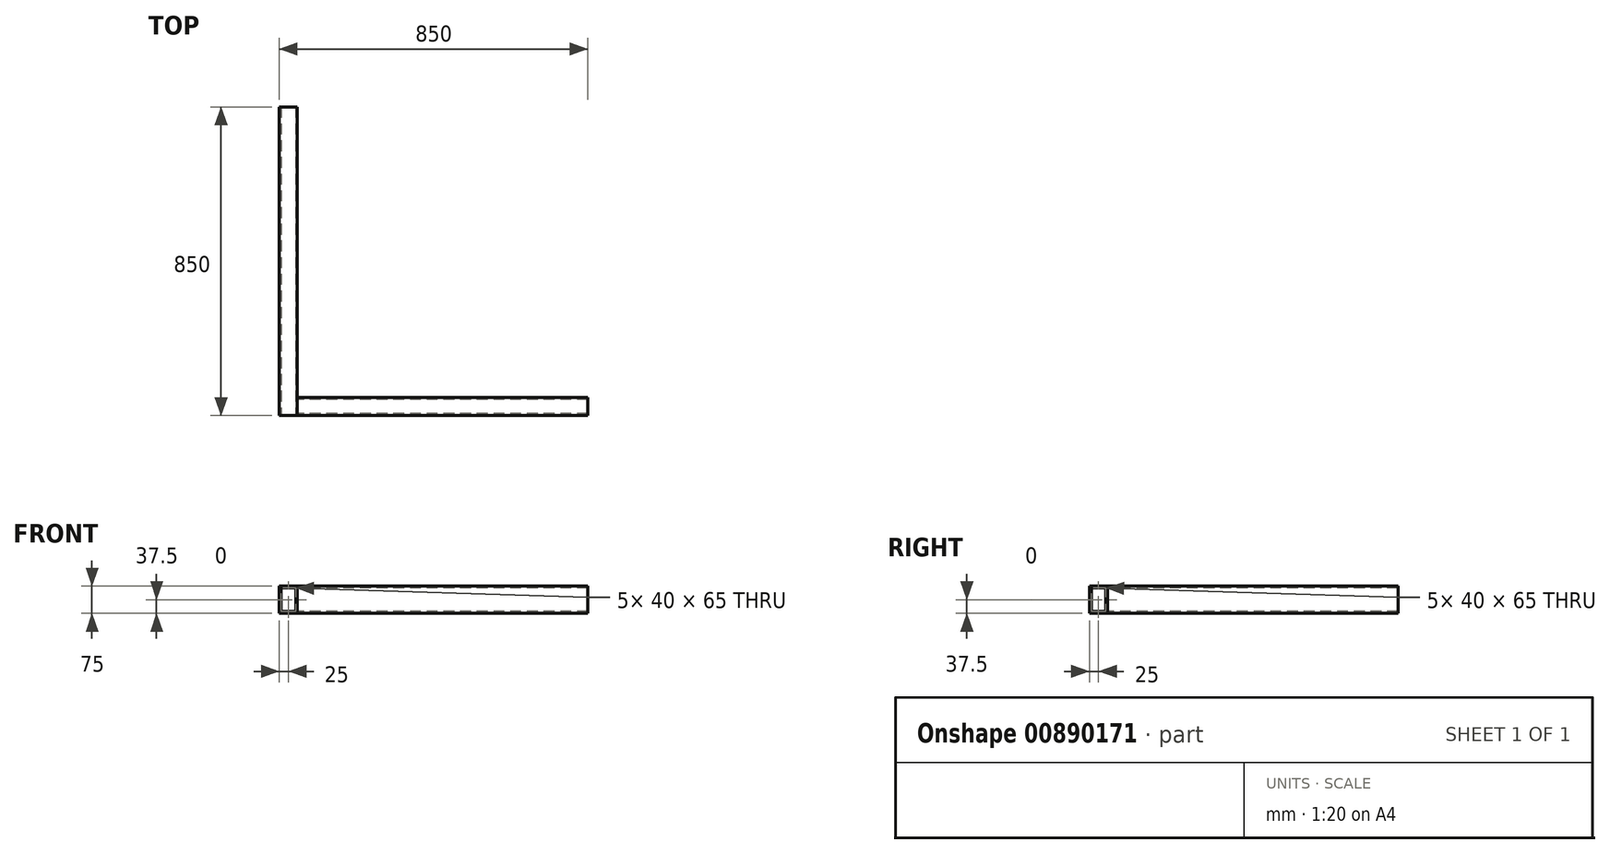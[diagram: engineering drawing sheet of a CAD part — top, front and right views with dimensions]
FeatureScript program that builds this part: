
annotation { "Feature Type Name" : "Feature", "Feature Type Description" : "" }
export const myFeature = defineFeature(function(context is Context, id is Id, definition is map)
    precondition{}
    {
        {
            var Q0;
            Q0=qCreatedBy(makeId("Front.planeOp"),FACE);
            var sketch = newSketch(context, id + "F0", { "sketchPlane" : qUnion([Q0])});
            skLineSegment(sketch, "E0.bottom", {"start": v(0, 0) * mm, "end": v(-50, 0) * mm});
            skLineSegment(sketch, "E0.top", {"start": v(0, 75) * mm, "end": v(-50, 75) * mm});
            skLineSegment(sketch, "E0.left", {"start": v(0, 0) * mm, "end": v(0, 75) * mm});
            skLineSegment(sketch, "E0.right", {"start": v(-50, 0) * mm, "end": v(-50, 75) * mm});
            skLineSegment(sketch, "E1.0", {"start": v(-5, 70) * mm, "end": v(-45, 70) * mm});
            skLineSegment(sketch, "E1.1", {"start": v(-5, 5) * mm, "end": v(-5, 70) * mm});
            skLineSegment(sketch, "E1.2", {"start": v(-5, 5) * mm, "end": v(-45, 5) * mm});
            skLineSegment(sketch, "E1.3", {"start": v(-45, 5) * mm, "end": v(-45, 70) * mm});
            skSolve(sketch);
        }
        {
            var Q0;
            Q0=makeQuery(id+"F0.imprint","IMPRINT",FACE,{"disambiguationData":[TD([[makeQuery(id+"F0.imprint","IMPRINT",EDGE,{"derivedFrom":sQuery(id+"F0.wireOp",EDGE,"E0.bottom")}),-1.0]])]});
            extrude(context, id + "F1", {"entities" : qUnion([Q0]), "oppositeDirection" : true, "depth" : 850 * mm, "offsetDistance" : 25 * mm});
        }
        {
            var Q0;
            Q0=qCreatedBy(makeId("Right.planeOp"),FACE);
            var sketch = newSketch(context, id + "F2", { "sketchPlane" : qUnion([Q0])});
            skLineSegment(sketch, "E2.bottom", {"start": v(0, 0) * mm, "end": v(50, 0) * mm});
            skLineSegment(sketch, "E2.top", {"start": v(0, 75) * mm, "end": v(50, 75) * mm});
            skLineSegment(sketch, "E2.left", {"start": v(0, 0) * mm, "end": v(0, 75) * mm});
            skLineSegment(sketch, "E2.right", {"start": v(50, 0) * mm, "end": v(50, 75) * mm});
            skLineSegment(sketch, "E3.0", {"start": v(5, 5) * mm, "end": v(5, 70) * mm});
            skLineSegment(sketch, "E3.1", {"start": v(5, 5) * mm, "end": v(45, 5) * mm});
            skLineSegment(sketch, "E3.2", {"start": v(45, 5) * mm, "end": v(45, 70) * mm});
            skLineSegment(sketch, "E3.3", {"start": v(5, 70) * mm, "end": v(45, 70) * mm});
            skSolve(sketch);
        }
        {
            var Q0;
            Q0=qSketchRegion(id+"F2",true);
            extrude(context, id + "F3", {"entities" : qUnion([Q0]), "depth" : 800 * mm, "offsetDistance" : 25 * mm});
        }
    });
